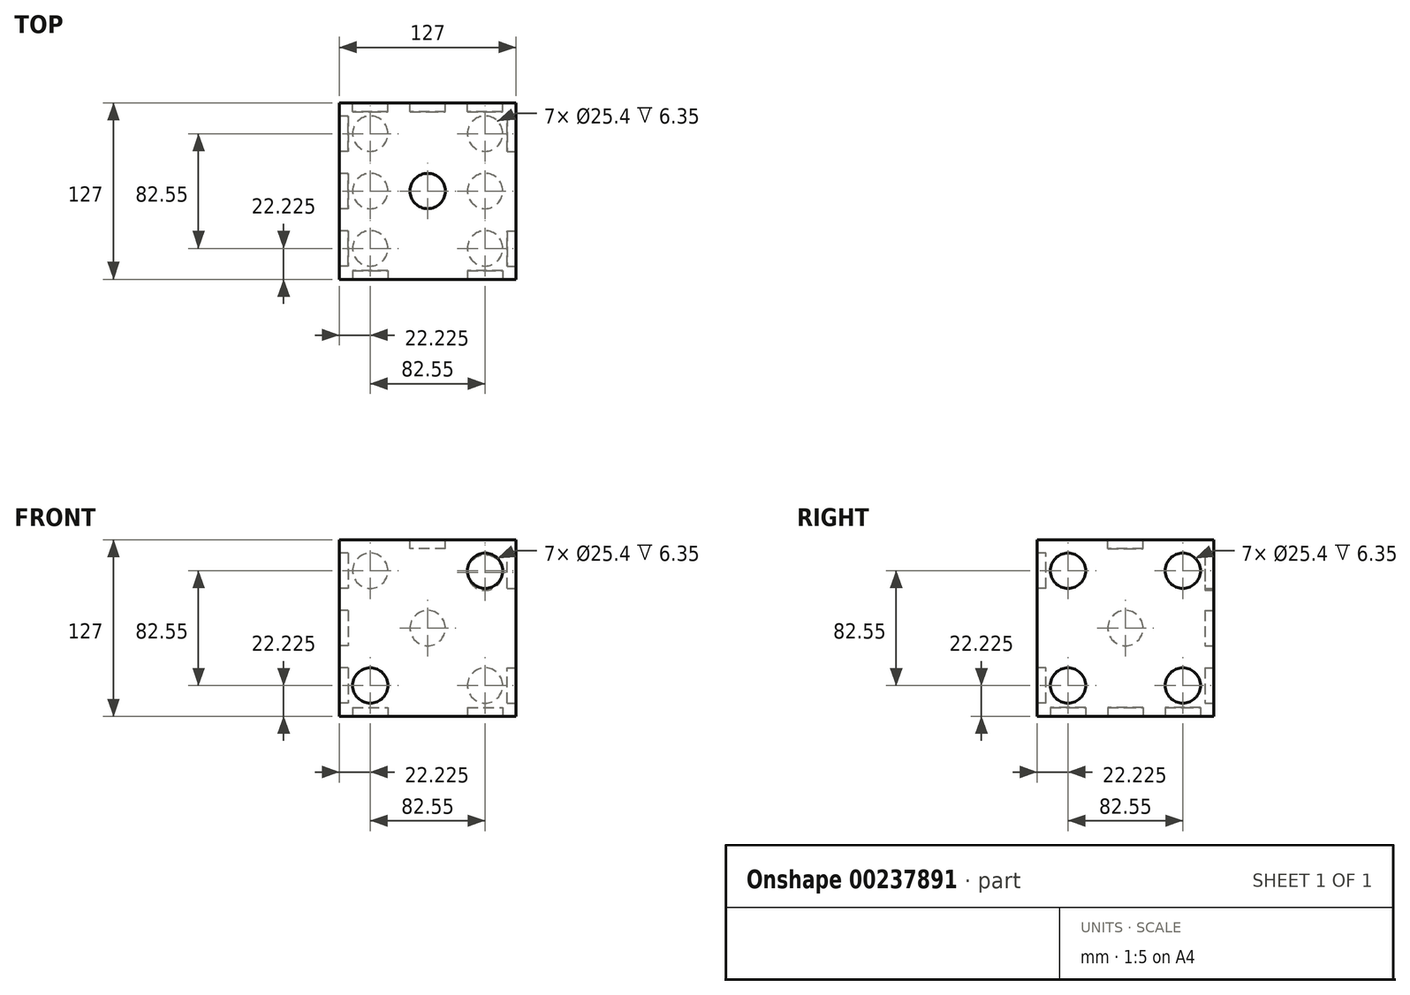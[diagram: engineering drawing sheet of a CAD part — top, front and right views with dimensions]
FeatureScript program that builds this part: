
annotation { "Feature Type Name" : "Feature", "Feature Type Description" : "" }
export const myFeature = defineFeature(function(context is Context, id is Id, definition is map)
    precondition{}
    {
        {
            var Q0;
            Q0=qCreatedBy(makeId("Top.planeOp"),FACE);
            var sketch = newSketch(context, id + "F0", { "sketchPlane" : qUnion([Q0])});
            skLineSegment(sketch, "E0.bottom", {"start": v(0, 0) * mm, "end": v(127, 0) * mm});
            skLineSegment(sketch, "E0.top", {"start": v(0, 127) * mm, "end": v(127, 127) * mm});
            skLineSegment(sketch, "E0.left", {"start": v(0, 0) * mm, "end": v(0, 127) * mm});
            skLineSegment(sketch, "E0.right", {"start": v(127, 0) * mm, "end": v(127, 127) * mm});
            skSolve(sketch);
        }
        {
            var Q0;
            Q0=makeQuery(id+"F0.imprint","IMPRINT",FACE,{"disambiguationData":[TD([[makeQuery(id+"F0.imprint","IMPRINT",EDGE,{"derivedFrom":sQuery(id+"F0.wireOp",EDGE,"E0.bottom")}),1.0]])]});
            extrude(context, id + "F1", {"entities" : qUnion([Q0]), "depth" : 127 * mm});
        }
        {
            var Q0;
            Q0=makeQuery(id+"F1.opExtrude","CAP_FACE",FACE,{"disambiguationData":[OSD([sQuery(id+"F0.wireOp",EDGE,"E0.bottom"),sQuery(id+"F0.wireOp",EDGE,"E0.top"),sQuery(id+"F0.wireOp",EDGE,"E0.left"),sQuery(id+"F0.wireOp",EDGE,"E0.right")])],"isStart":false});
            var sketch = newSketch(context, id + "F2", { "sketchPlane" : qUnion([Q0])});
            skCircle(sketch, "E1", {"center": v(63.5, 63.5) * mm, "radius": 12.7 * mm});
            skSolve(sketch);
        }
        {
            var Q0;
            Q0=makeQuery(id+"F2.imprint","IMPRINT",FACE,{"disambiguationData":[TD([[makeQuery(id+"F2.imprint","IMPRINT",EDGE,{"derivedFrom":sQuery(id+"F2.wireOp",EDGE,"E1")}),1.0]])]});
            extrude(context, id + "F3", {"entities" : qUnion([Q0]), "operationType" : NewBodyOperationType.REMOVE, "oppositeDirection" : true, "depth" : 6.35 * mm});
        }
        {
            var Q0;
            Q0=makeQuery(id+"F1.opExtrude","SWEPT_FACE",FACE,{"disambiguationData":[OSD([sQuery(id+"F0.wireOp",EDGE,"E0.bottom")])]});
            var sketch = newSketch(context, id + "F4", { "sketchPlane" : qUnion([Q0])});
            skCircle(sketch, "E2", {"center": v(22.23, 22.22) * mm, "radius": 12.7 * mm});
            skCircle(sketch, "E3", {"center": v(104.78, 104.78) * mm, "radius": 12.7 * mm});
            skSolve(sketch);
        }
        {
            var Q0;
            Q0=makeQuery(id+"F4.imprint","IMPRINT",FACE,{"disambiguationData":[TD([[makeQuery(id+"F4.imprint","IMPRINT",EDGE,{"derivedFrom":sQuery(id+"F4.wireOp",EDGE,"E2")}),1.0]])]});
            var Q1;
            Q1=makeQuery(id+"F4.imprint","IMPRINT",FACE,{"disambiguationData":[TD([[makeQuery(id+"F4.imprint","IMPRINT",EDGE,{"derivedFrom":sQuery(id+"F4.wireOp",EDGE,"E3")}),1.0]])]});
            extrude(context, id + "F5", {"entities" : qUnion([Q0, Q1]), "operationType" : NewBodyOperationType.REMOVE, "oppositeDirection" : true, "depth" : 6.35 * mm});
        }
        {
            var Q0;
            Q0=makeQuery(id+"F1.opExtrude","SWEPT_FACE",FACE,{"disambiguationData":[OSD([sQuery(id+"F0.wireOp",EDGE,"E0.left")])]});
            var sketch = newSketch(context, id + "F6", { "sketchPlane" : qUnion([Q0])});
            skLineSegment(sketch, "E4", {"start": v(-127, 0) * mm, "end": v(0, 127) * mm, "construction": true});
            skCircle(sketch, "E5", {"center": v(-104.77, 22.23) * mm, "radius": 12.7 * mm});
            skCircle(sketch, "E6", {"center": v(-63.5, 63.5) * mm, "radius": 12.7 * mm});
            skCircle(sketch, "E7", {"center": v(-22.22, 104.78) * mm, "radius": 12.7 * mm});
            skSolve(sketch);
        }
        {
            var Q0;
            Q0 = qSketchRegion(id + "F6", true);
            extrude(context, id + "F7", {"entities" : qUnion([Q0]), "operationType" : NewBodyOperationType.REMOVE, "oppositeDirection" : true, "depth" : 6.35 * mm});
        }
        {
            var Q0;
            Q0=makeQuery(id+"F1.opExtrude","SWEPT_FACE",FACE,{"disambiguationData":[OSD([sQuery(id+"F0.wireOp",EDGE,"E0.right")])]});
            var sketch = newSketch(context, id + "F8", { "sketchPlane" : qUnion([Q0])});
            skCircle(sketch, "E8", {"center": v(22.22, 22.22) * mm, "radius": 12.7 * mm});
            skCircle(sketch, "E9", {"center": v(104.77, 104.78) * mm, "radius": 12.7 * mm});
            skCircle(sketch, "E10", {"center": v(22.22, 104.78) * mm, "radius": 12.7 * mm});
            skCircle(sketch, "E11", {"center": v(104.77, 22.22) * mm, "radius": 12.7 * mm});
            skSolve(sketch);
        }
        {
            var Q0;
            Q0=makeQuery(id+"F8.imprint","IMPRINT",FACE,{"disambiguationData":[TD([[makeQuery(id+"F8.imprint","IMPRINT",EDGE,{"derivedFrom":sQuery(id+"F8.wireOp",EDGE,"E10")}),1.0]])]});
            var Q1;
            Q1=makeQuery(id+"F8.imprint","IMPRINT",FACE,{"disambiguationData":[TD([[makeQuery(id+"F8.imprint","IMPRINT",EDGE,{"derivedFrom":sQuery(id+"F8.wireOp",EDGE,"E9")}),1.0]])]});
            var Q2;
            Q2=makeQuery(id+"F8.imprint","IMPRINT",FACE,{"disambiguationData":[TD([[makeQuery(id+"F8.imprint","IMPRINT",EDGE,{"derivedFrom":sQuery(id+"F8.wireOp",EDGE,"E11")}),1.0]])]});
            var Q3;
            Q3=makeQuery(id+"F8.imprint","IMPRINT",FACE,{"disambiguationData":[TD([[makeQuery(id+"F8.imprint","IMPRINT",EDGE,{"derivedFrom":sQuery(id+"F8.wireOp",EDGE,"E8")}),1.0]])]});
            extrude(context, id + "F9", {"entities" : qUnion([Q0, Q1, Q2, Q3]), "operationType" : NewBodyOperationType.REMOVE, "oppositeDirection" : true, "depth" : 6.35 * mm});
        }
        {
            var Q0;
            Q0=makeQuery(id+"F1.opExtrude","CAP_FACE",FACE,{"disambiguationData":[OSD([sQuery(id+"F0.wireOp",EDGE,"E0.bottom"),sQuery(id+"F0.wireOp",EDGE,"E0.top"),sQuery(id+"F0.wireOp",EDGE,"E0.left"),sQuery(id+"F0.wireOp",EDGE,"E0.right")])],"isStart":true});
            var sketch = newSketch(context, id + "F10", { "sketchPlane" : qUnion([Q0])});
            skCircle(sketch, "E12", {"center": v(22.23, -22.23) * mm, "radius": 12.7 * mm});
            skCircle(sketch, "E13", {"center": v(22.23, -104.78) * mm, "radius": 12.7 * mm});
            skCircle(sketch, "E14", {"center": v(104.78, -22.23) * mm, "radius": 12.7 * mm});
            skCircle(sketch, "E15", {"center": v(104.77, -104.78) * mm, "radius": 12.7 * mm});
            skCircle(sketch, "E16", {"center": v(22.23, -63.5) * mm, "radius": 12.7 * mm});
            skCircle(sketch, "E17", {"center": v(104.77, -63.5) * mm, "radius": 12.7 * mm});
            skSolve(sketch);
        }
        {
            var Q0;
            Q0 = qSketchRegion(id + "F10", true);
            extrude(context, id + "F11", {"entities" : qUnion([Q0]), "operationType" : NewBodyOperationType.REMOVE, "oppositeDirection" : true, "depth" : 6.35 * mm});
        }
        {
            var Q0;
            Q0=makeQuery(id+"F1.opExtrude","SWEPT_FACE",FACE,{"disambiguationData":[OSD([sQuery(id+"F0.wireOp",EDGE,"E0.top")])]});
            var sketch = newSketch(context, id + "F12", { "sketchPlane" : qUnion([Q0])});
            skCircle(sketch, "E18", {"center": v(-104.77, 22.22) * mm, "radius": 12.7 * mm});
            skCircle(sketch, "E19", {"center": v(-63.5, 63.5) * mm, "radius": 12.7 * mm});
            skCircle(sketch, "E20", {"center": v(-104.77, 103.4) * mm, "radius": 12.7 * mm});
            skCircle(sketch, "E21", {"center": v(-22.23, 104.78) * mm, "radius": 12.7 * mm});
            skCircle(sketch, "E22", {"center": v(-22.23, 22.22) * mm, "radius": 12.7 * mm});
            skSolve(sketch);
        }
        {
            var Q0;
            Q0=makeQuery(id+"F12.imprint","IMPRINT",FACE,{"disambiguationData":[TD([[makeQuery(id+"F12.imprint","IMPRINT",EDGE,{"derivedFrom":sQuery(id+"F12.wireOp",EDGE,"E20")}),1.0]])]});
            var Q1;
            Q1=makeQuery(id+"F12.imprint","IMPRINT",FACE,{"disambiguationData":[TD([[makeQuery(id+"F12.imprint","IMPRINT",EDGE,{"derivedFrom":sQuery(id+"F12.wireOp",EDGE,"E19")}),1.0]])]});
            var Q2;
            Q2=makeQuery(id+"F12.imprint","IMPRINT",FACE,{"disambiguationData":[TD([[makeQuery(id+"F12.imprint","IMPRINT",EDGE,{"derivedFrom":sQuery(id+"F12.wireOp",EDGE,"E21")}),1.0]])]});
            var Q3;
            Q3=makeQuery(id+"F12.imprint","IMPRINT",FACE,{"disambiguationData":[TD([[makeQuery(id+"F12.imprint","IMPRINT",EDGE,{"derivedFrom":sQuery(id+"F12.wireOp",EDGE,"E22")}),1.0]])]});
            var Q4;
            Q4=makeQuery(id+"F12.imprint","IMPRINT",FACE,{"disambiguationData":[TD([[makeQuery(id+"F12.imprint","IMPRINT",EDGE,{"derivedFrom":sQuery(id+"F12.wireOp",EDGE,"E18")}),1.0]])]});
            extrude(context, id + "F13", {"entities" : qUnion([Q0, Q1, Q2, Q3, Q4]), "operationType" : NewBodyOperationType.REMOVE, "oppositeDirection" : true, "depth" : 6.35 * mm});
        }
    });
